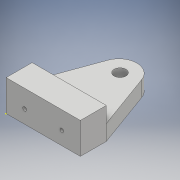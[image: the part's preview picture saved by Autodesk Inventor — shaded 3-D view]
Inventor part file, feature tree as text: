
AUTODESK INVENTOR PART (.ipt)
format: ipt  version: 2017 (Build 210142000, 142)  size: 128,512 bytes
history: native  units: mm
features: sketch x5, extrude x3
ambient origin geometry x8: Origin, YZ Plane, XZ Plane, XY Plane, X Axis, Y Axis, Z Axis, Center Point
bodies: Solid1 (feature_tree)
feature tree (8):
  sketch  "Sketch1"  dims[d9=4.2mm d10=0.0mm d11=4.2mm d12=0.0mm]
  sketch  "Sketch2"  dims[d13=1.0mm d14=1.0mm]
  sketch  "Sketch3"  dims[d15=5.5mm d16=0.0mm d17=7.0mm]
  extrude  "Extrusion1"  Depth=4.2mm TaperAngle=0.0deg
  extrude  "Extrusion2"  Depth=1.0mm
  extrude  "Extrusion3"  Depth=7.0mm
  sketch  "Sketch4"  dims[d18=6.999813mm]
  sketch  "Sketch5"  dims[d19=20.7mm d23=90.0deg d24=90.0deg d25=10.0mm d26=16.0mm d27=12.217305mm d28=16.0mm d29=19.198622mm d30=10.0mm d33=4.8mm d34=4.8mm]
